# Revit family: Electronics_Community-Point-Source_Biamp_Loudspeaker_R_35COAX
name_source: partatom
category: Communication Devices
units: mm (PartAtom-declared; Revit-internal decimal feet)

## family parameters
Cut with Voids When Loaded = No
Host = Face
Maintain Annotation Orientation = No
OmniClass Number = 23.85.10.11.14.14.14
OmniClass Title = Loudspeakers
Part Type = Normal
Room Calculation Point = No
Round Connector Dimension = Use Diameter
Shared = No

## types (2) — shared parameters
Connector Description = NL4, 2-position terminal strip; Low Impedance 8 ohm, 70V/100V operation
Controls = Music / Voice switch, 70V/100V operation jumper
Default Elevation = 48 "
Depth = 13.5 "
Description = R.35COAX Two-Way 10-Inch Coaxial Weather-Resistant Loudspeaker
Environmental = IP55W per IEC 529, designed to MIL-STD-810G Color-matched ABS plastic input panel weather cover with 13.5mm ID gland nut installed in .82 knockout
Equalized Maximum SPL = MUSIC - Peak - 126dB; Continuous - 120dB
Equalized Sensitivity = MUSIC - 1W - 97dB; 2.83V - 97dB
Finish = Refer to the Technical Drawing (page 3)
Height = 10.98 "
Included Accessories = Zinc-rich epoxy dual-layer powder-coated yoke, included integral safety cable mounting point
Input Connection = NL4 Speakon-type connector (low impedance only), and 7-position terminal strip for low impedance or constant voltage operation
Manufacturer = Biamp
Mounting Points = Two (2) M8 rigging points
Nominal Beamwidth  (H x V) = 90° x 90°
Nominal Maximum SPL (Whole Space) = MUSIC - Peak - 126dB; Continuous - 120dB. VOICE - Peak - 128dB; Continuous - 122dB
Nominal Sensitivity = MUSIC - 1W - 97dB; 2.83V - 97dB. VOICE - 1W - 99dB; 2.83V - 99dB
Operating Environment = Indoor or Weather-Resistant Outdoor
Operating Mode = Passive, Selectable Low Impedance or 70V/100V
Operating Range = 70 Hz to 16 kHz
Product Documentation Link = https://downloads.biamp.com
Product Page URL = https://www.biamp.com
Product data url = https://www.bimobject.com
Recommended Amplifers = 200W - 400W @ 8 Ohms,  (40V - 57V)
Required Accessories = High Pass Filter - 70 Hz, 24 dB /octave, Digital Signal Processor
Transducers = LF   1 x 10 (254mm) Carbon ring cone with hydrophobic treatment, 2 (51mm) Voice Coil HF  1 x 1.25 (32mm) exit compression
URL = https://www.biamp.com
Weight = 26.01 lb
Width = 12.99 "

## per-type parameters (varying)
| type | Grill Material | Housing Material | Yoke Material |
| R.35COAX B | Biamp - Plastic - Black(Grid) | Biamp - Plastic - Black | Biamp - Metal - Black |
| R.35COAX G | Biamp - Plastic - Gray(Grid) | Biamp - Plastic - Gray | Biamp - Metal - Gray |

note: column(s) folded — value = type name in every type: Model

## geometry (parser evidence)
native form markers: Sweep x5
no freeform markers — native parametric forms only
